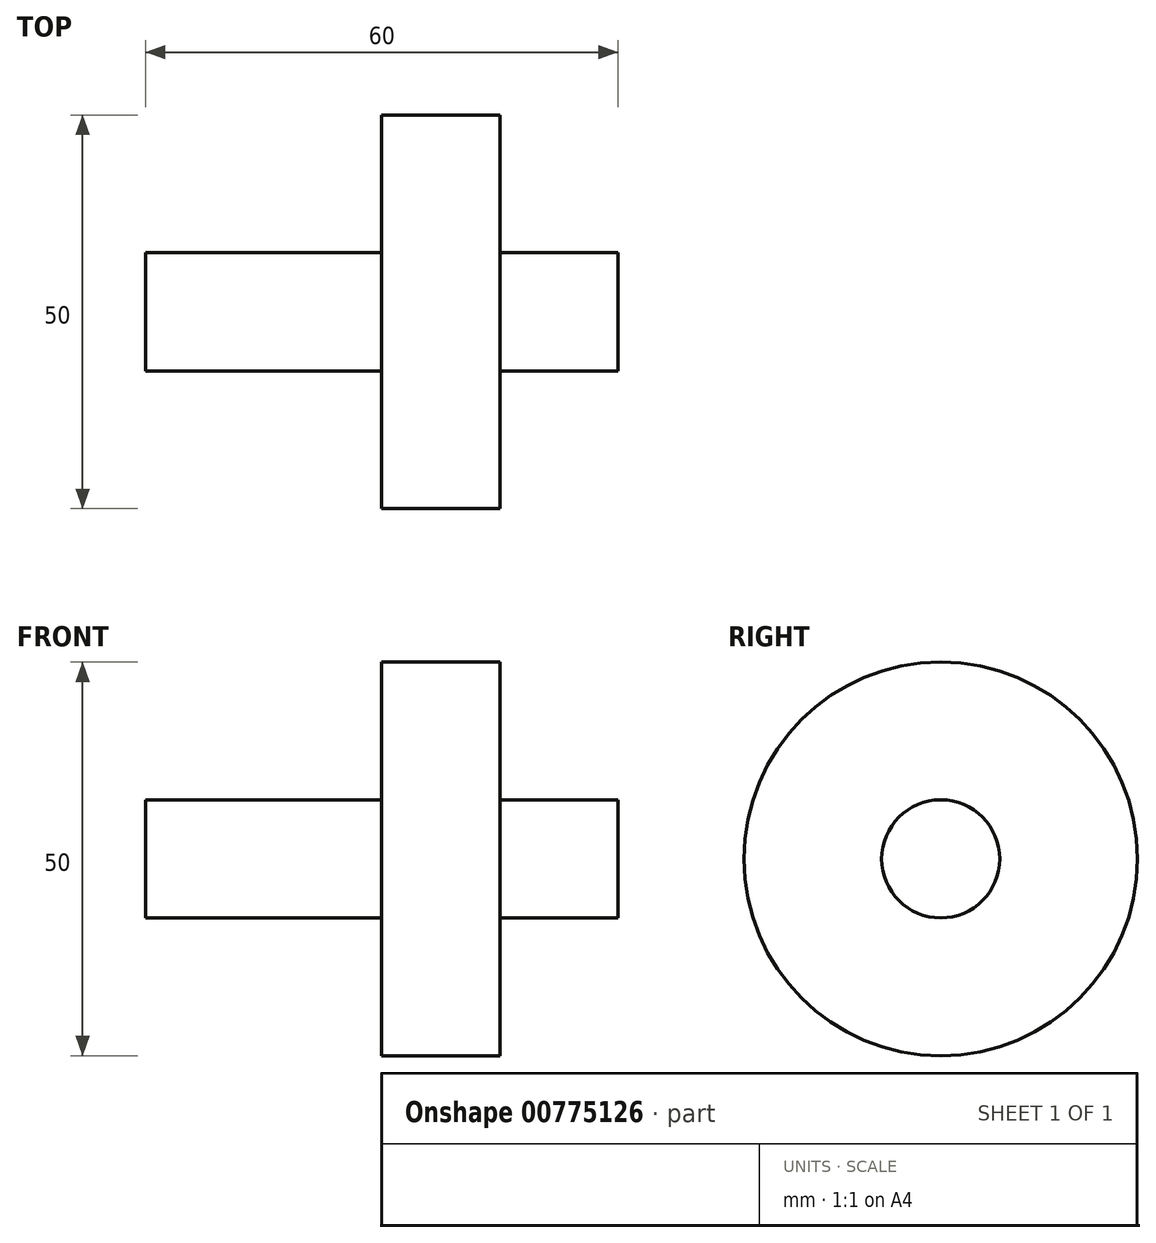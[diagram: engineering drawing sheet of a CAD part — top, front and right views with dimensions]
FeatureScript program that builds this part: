
annotation { "Feature Type Name" : "Feature", "Feature Type Description" : "" }
export const myFeature = defineFeature(function(context is Context, id is Id, definition is map)
    precondition{}
    {
        {
            var Q0;
            Q0=qCreatedBy(makeId("Top.planeOp"),FACE);
            var sketch = newSketch(context, id + "F0", { "sketchPlane" : qUnion([Q0])});
            skLineSegment(sketch, "E0", {"start": v(0, 0) * mm, "end": v(-15, 0) * mm});
            skLineSegment(sketch, "E1", {"start": v(-15, 0) * mm, "end": v(-30, 0) * mm});
            skLineSegment(sketch, "E2", {"start": v(-30, 0) * mm, "end": v(-60, 0) * mm});
            skLineSegment(sketch, "E3", {"start": v(-60, 0) * mm, "end": v(-60, -7.5) * mm});
            skLineSegment(sketch, "E4", {"start": v(0, 0) * mm, "end": v(0, -7.5) * mm});
            skLineSegment(sketch, "E5", {"start": v(-30, -7.5) * mm, "end": v(-30, -25) * mm});
            skLineSegment(sketch, "E6", {"start": v(-30, -25) * mm, "end": v(-15, -25) * mm});
            skLineSegment(sketch, "E7", {"start": v(-15, -25) * mm, "end": v(-15, -7.5) * mm});
            skLineSegment(sketch, "E8", {"start": v(-60, -7.5) * mm, "end": v(-30, -7.5) * mm});
            skLineSegment(sketch, "E9.trimOffspring", {"start": v(-15, -7.5) * mm, "end": v(0, -7.5) * mm});
            skSolve(sketch);
        }
        {
            var Q0;
            Q0 = qSketchRegion(id + "F0", true);
            var Q1;
            Q1=sQuery(id+"F0.wireOp",EDGE,"E1");
            revolve(context, id + "F1", {"surfaceOperationType" : NewSurfaceOperationType.NEW, "entities" : qUnion([Q0]), "axis" : qUnion([Q1]), "revolveType" : RevolveType.FULL});
        }
    });
